# Revit family: Door-Access-Cendrex-Flush_Aluminum_Floor_Hatch-PPA
name_source: partatom
category: Specialty Equipment
revit_build: Autodesk Revit Architecture 2013 (Build: 20130531_2115(x64)
units: mm (PartAtom-declared; Revit-internal decimal feet)

## types (3) — shared parameters
Assembly Code = C1020700
Available Options = http://cendrex.com
Cendrex LEED Ready Program = http://www.cendrex.com
Construction Material = Metal - Cendrex - Aluminum
Default Elevation = 0"
Description = PPA - Flush Aluminum Floor Hatch
Door Open = No
Door Swing = 0.00°
Door Width = 24"
Finish = Metal - Cendrex - Powder Coated White
Frame Depth = 1 3/4"
Manufacturer = Cendrex
Model = PPA
Product Documentation Link = http://cendrex.com
Product Page URL = http://www.cendrex.com
URL = http://www.cendrex.com
Width Actual = 28"
Width Calc = 24"

## per-type parameters (varying)
| type | Diamond Plate | Door Height | Height Actual | Height Calc |
| Custom | <By Category> | 24" | 28 1/32" | 24" |
| 24x24 | Metal - Cendrex - Aluminum Diamond Plate | 24" | 28 1/32" | 24" |
| 24x36 | <By Category> | 36" | 40 1/32" | 36" |

## geometry (parser evidence)
native form markers: Blend x22, Sweep x10
no freeform markers — native parametric forms only
